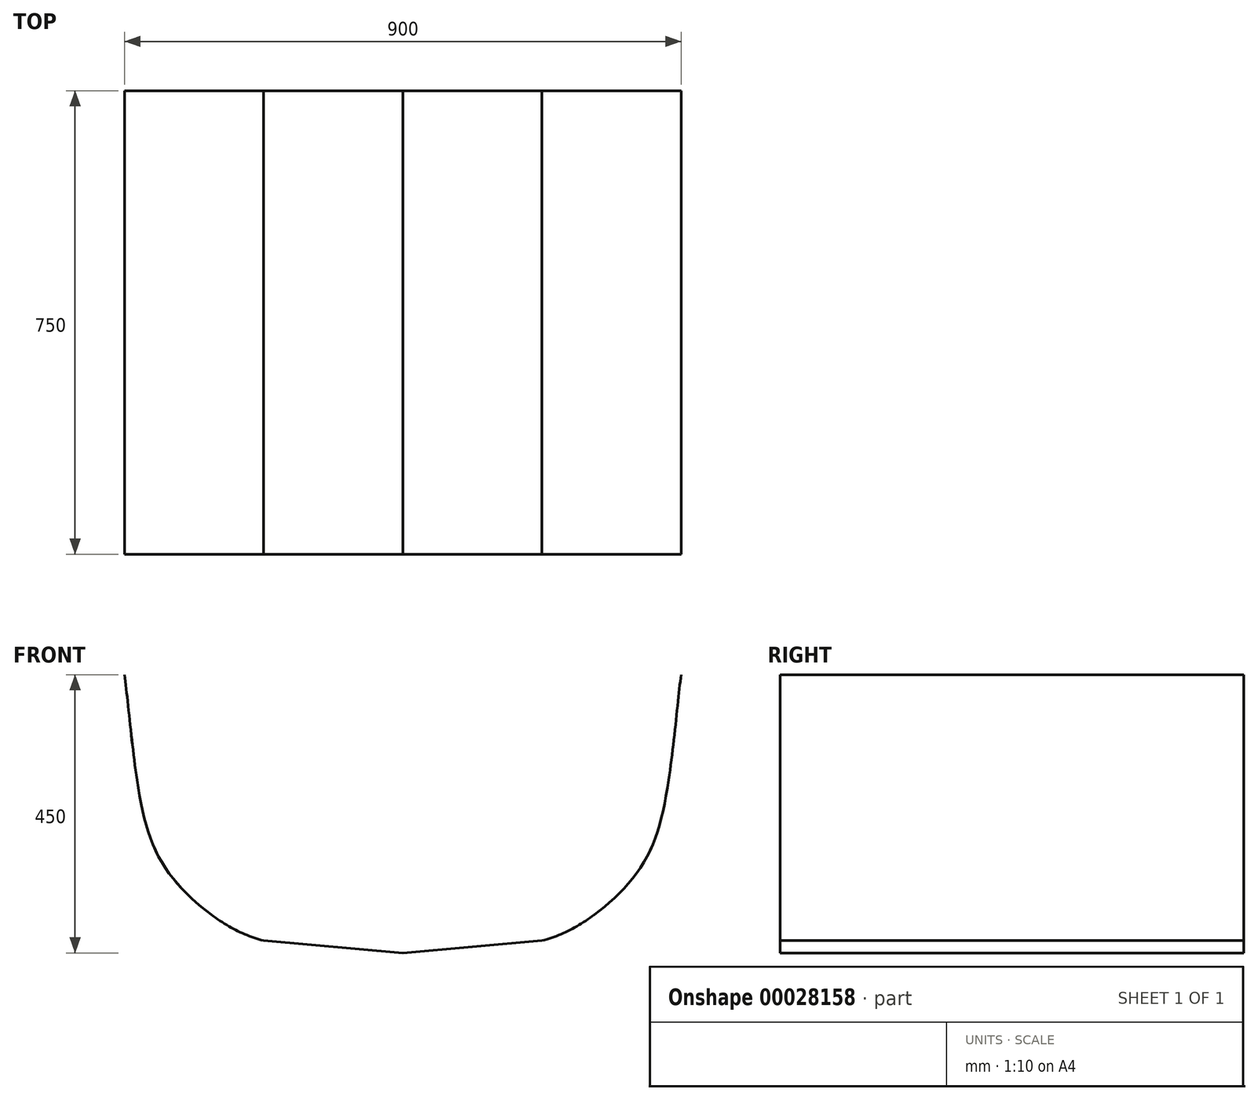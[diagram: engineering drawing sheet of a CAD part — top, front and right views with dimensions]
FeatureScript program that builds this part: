
annotation { "Feature Type Name" : "Feature", "Feature Type Description" : "" }
export const myFeature = defineFeature(function(context is Context, id is Id, definition is map)
    precondition{}
    {
        {
            var Q0;
            Q0=qCreatedBy(makeId("Front.planeOp"),FACE);
            var sketch = newSketch(context, id + "F0", { "sketchPlane" : qUnion([Q0])});
            skLineSegment(sketch, "E0.rect.bottom", {"start": v(450, -225) * mm, "end": v(-450, -225) * mm, "construction": true});
            skLineSegment(sketch, "E0.rect.top", {"start": v(450, 225) * mm, "end": v(-450, 225) * mm, "construction": true});
            skLineSegment(sketch, "E0.rect.left", {"start": v(450, -225) * mm, "end": v(450, 225) * mm, "construction": true});
            skLineSegment(sketch, "E0.rect.right", {"start": v(-450, -225) * mm, "end": v(-450, 225) * mm, "construction": true});
            skPoint(sketch, "E0.rect.middle", {"position": v(0, 0) * mm});
            skLineSegment(sketch, "E1", {"start": v(0, 225) * mm, "end": v(0, -225) * mm, "construction": true});
            skFitSpline(sketch, "E2", {"points": [v(225, -205) * mm, v(310, -163.17) * mm, v(390, -78.07) * mm, v(430, 55) * mm, v(450, 225) * mm], "startDerivative": vector(427.72, 105.03) * mm, "endDerivative": vector(49.91, 392.93) * mm});
            skLineSegment(sketch, "E3", {"start": v(0, -225) * mm, "end": v(225, -205) * mm});
            skLineSegment(sketch, "E4.MirrorCS", {"start": v(0, -225) * mm, "end": v(-225, -205) * mm});
            skFitSpline(sketch, "E5.MirrorCS", {"points": [v(-225, -205) * mm, v(-310, -163.17) * mm, v(-390, -78.07) * mm, v(-430, 55) * mm, v(-450, 225) * mm], "startDerivative": vector(-427.72, 105.03) * mm, "endDerivative": vector(-49.91, 392.93) * mm});
            skSolve(sketch);
        }
        {
            var Q0;
            Q0=qCreatedBy(makeId("Front.planeOp"),FACE);
            cPlane(context, id + "F1", {"entities" : qUnion([Q0]), "cplaneType" : CPlaneType.OFFSET, "offset" : 750 * mm, "width" : 150 * mm, "height" : 150 * mm});
        }
        {
            var Q0;
            Q0=qCreatedBy(id+"F1.planeOp",FACE);
            var sketch = newSketch(context, id + "F2", { "sketchPlane" : qUnion([Q0])});
            skLineSegment(sketch, "E6.rect.bottom", {"start": v(450, -225) * mm, "end": v(-450, -225) * mm, "construction": true});
            skLineSegment(sketch, "E6.rect.top", {"start": v(450, 225) * mm, "end": v(-450, 225) * mm, "construction": true});
            skLineSegment(sketch, "E6.rect.left", {"start": v(450, -225) * mm, "end": v(450, 225) * mm, "construction": true});
            skLineSegment(sketch, "E6.rect.right", {"start": v(-450, -225) * mm, "end": v(-450, 225) * mm, "construction": true});
            skPoint(sketch, "E6.rect.middle", {"position": v(0, 0) * mm});
            skLineSegment(sketch, "E7", {"start": v(0, 225) * mm, "end": v(0, -225) * mm, "construction": true});
            skFitSpline(sketch, "E8", {"points": [v(225, -205) * mm, v(310, -163.17) * mm, v(390, -78.28) * mm, v(430, 55) * mm, v(450, 225) * mm], "startDerivative": vector(427.72, 105.03) * mm, "endDerivative": vector(49.91, 392.93) * mm});
            skLineSegment(sketch, "E9", {"start": v(0, -225) * mm, "end": v(225, -205) * mm});
            skLineSegment(sketch, "E10.MirrorCS", {"start": v(0, -225) * mm, "end": v(-225, -205) * mm});
            skFitSpline(sketch, "E11.MirrorCS", {"points": [v(-225, -205) * mm, v(-310, -163.17) * mm, v(-390, -78.28) * mm, v(-430, 55) * mm, v(-450, 225) * mm], "startDerivative": vector(-427.72, 105.03) * mm, "endDerivative": vector(-49.91, 392.93) * mm});
            skSolve(sketch);
        }
        {
            var Q0;
            Q0=qCreatedBy(makeId("Front.planeOp"),FACE);
            cPlane(context, id + "F3", {"entities" : qUnion([Q0]), "cplaneType" : CPlaneType.OFFSET, "offset" : 1250 * mm, "width" : 150 * mm, "height" : 150 * mm});
        }
        {
            var Q0;
            Q0=sQuery(id+"F0.wireOp",EDGE,"E2");
            var Q1;
            Q1=sQuery(id+"F2.wireOp",EDGE,"E8");
            loft(context, id + "F4", {"bodyType" : ToolBodyType.SURFACE, "wireProfilesArray" : [{ "wireProfileEntities" : qUnion([Q0]) }, { "wireProfileEntities" : qUnion([Q1]) }]});
        }
        {
            var Q0;
            Q0=sQuery(id+"F0.wireOp",EDGE,"E3");
            var Q1;
            Q1=sQuery(id+"F2.wireOp",EDGE,"E9");
            loft(context, id + "F5", {"bodyType" : ToolBodyType.SURFACE, "wireProfilesArray" : [{ "wireProfileEntities" : qUnion([Q0]) }, { "wireProfileEntities" : qUnion([Q1]) }]});
        }
        {
            var Q0;
            Q0=sQuery(id+"F0.wireOp",EDGE,"E4.MirrorCS");
            var Q1;
            Q1=sQuery(id+"F2.wireOp",EDGE,"E10.MirrorCS");
            loft(context, id + "F6", {"bodyType" : ToolBodyType.SURFACE, "wireProfilesArray" : [{ "wireProfileEntities" : qUnion([Q0]) }, { "wireProfileEntities" : qUnion([Q1]) }]});
        }
        {
            var Q0;
            Q0=sQuery(id+"F0.wireOp",EDGE,"E5.MirrorCS");
            var Q1;
            Q1=sQuery(id+"F2.wireOp",EDGE,"E11.MirrorCS");
            loft(context, id + "F7", {"bodyType" : ToolBodyType.SURFACE, "wireProfilesArray" : [{ "wireProfileEntities" : qUnion([Q0]) }, { "wireProfileEntities" : qUnion([Q1]) }]});
        }
    });
